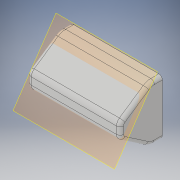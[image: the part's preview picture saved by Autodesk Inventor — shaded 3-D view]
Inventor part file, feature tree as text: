
AUTODESK INVENTOR PART (.ipt)
format: ipt  version: 2018 (Build 220112000, 112)  size: 187,904 bytes
history: native  units: in
note: dims shown in document units (in); Inventor stores cm internally (conversion verified against a paired STEP export)
features: fillet x3, sketch x3, extrude x2, shell x1, plane x1
ambient origin geometry x8: Origin, YZ Plane, XZ Plane, XY Plane, X Axis, Y Axis, Z Axis, Center Point
bodies: Solid1 (feature_tree)
feature tree (10):
  extrude  "Extrusion1"  Depth=3.5in
  shell  "Shell1"  Thickness=0.5in
  extrude  "Extrusion2"  Depth=7.6772in TaperAngle=0.0deg
  fillet  "Fillet4"  Radius=0.25in
  fillet  "Fillet5"  Radius=0.25in
  fillet  "Fillet6"  Radius=0.25in
  plane  "Work Plane1"
  sketch  "Sketch3"  dims[d9=0.25in d10=0.25in d11=7.6772in d12=0.0in d13=1.0in d14=1.0in d18=0.5906in d19=0.315in d20=1.1811in d21=90.0deg]
  sketch  "Sketch1"  dims[d0=4.4094in d1=3.5in d2=0.5in]
  sketch  "Sketch2"  dims[d3=0.5in d4=7.6772in d5=0.0in d6=0.25in d7=0.25in d8=0.25in]
